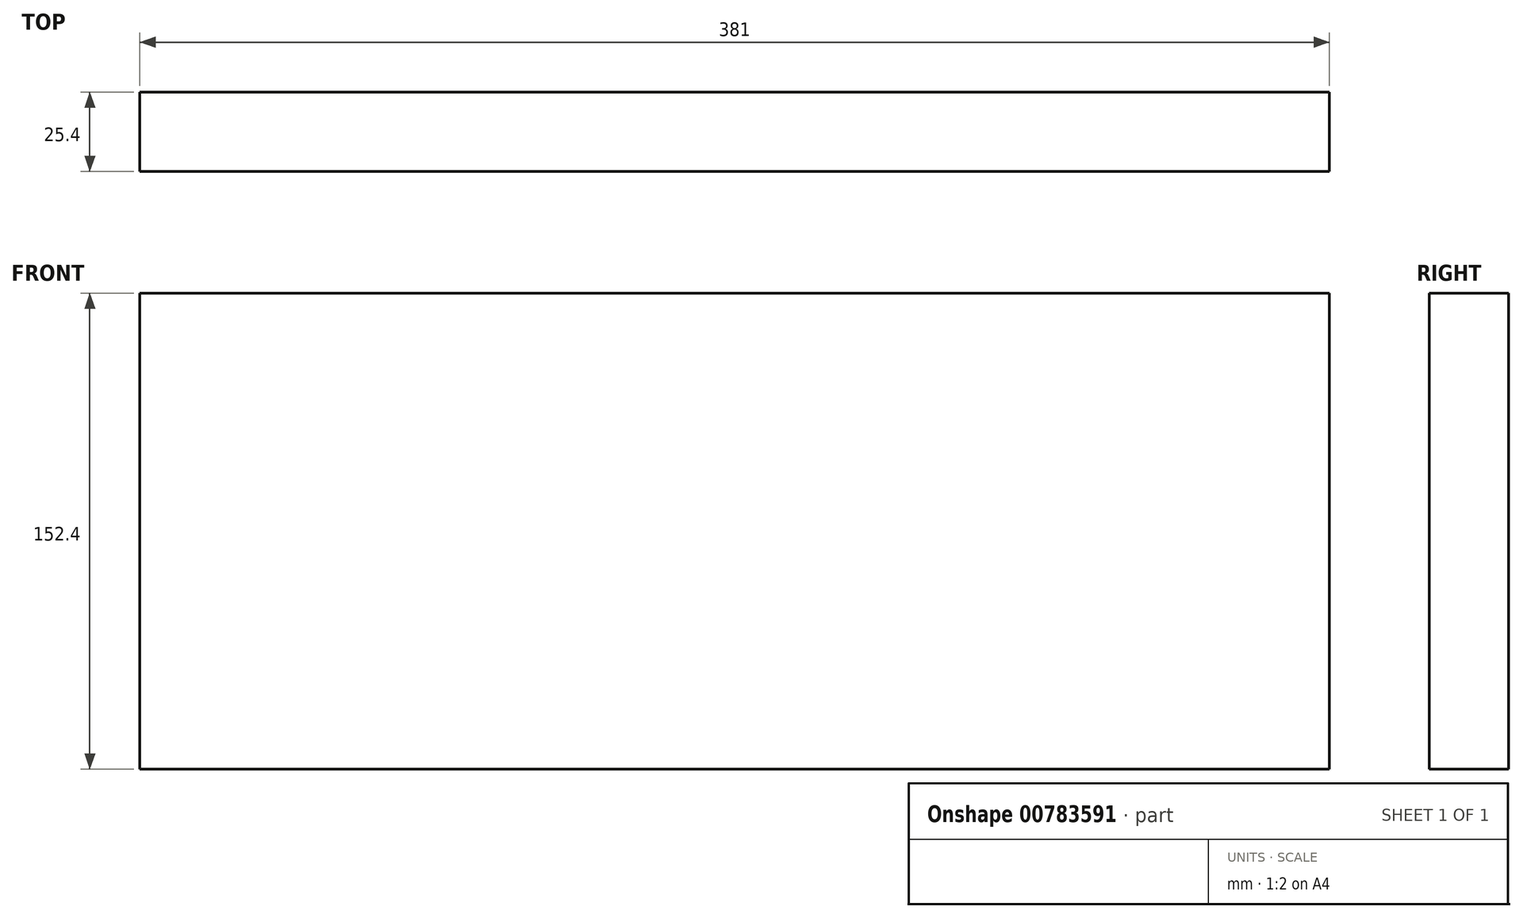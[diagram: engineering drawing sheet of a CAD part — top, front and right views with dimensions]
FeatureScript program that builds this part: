
annotation { "Feature Type Name" : "Feature", "Feature Type Description" : "" }
export const myFeature = defineFeature(function(context is Context, id is Id, definition is map)
    precondition{}
    {
        {
            var Q0;
            Q0=qCreatedBy(makeId("Front.planeOp"),FACE);
            var sketch = newSketch(context, id + "F0", { "sketchPlane" : qUnion([Q0])});
            skLineSegment(sketch, "E0.bottom", {"start": v(0, 0) * mm, "end": v(381, 0) * mm});
            skLineSegment(sketch, "E0.top", {"start": v(0, 152.4) * mm, "end": v(381, 152.4) * mm});
            skLineSegment(sketch, "E0.left", {"start": v(0, 0) * mm, "end": v(0, 152.4) * mm});
            skLineSegment(sketch, "E0.right", {"start": v(381, 0) * mm, "end": v(381, 152.4) * mm});
            skSolve(sketch);
        }
        {
            var Q0;
            Q0=makeQuery(id+"F0.imprint","IMPRINT",FACE,{"disambiguationData":[TD([[makeQuery(id+"F0.imprint","IMPRINT",EDGE,{"derivedFrom":sQuery(id+"F0.wireOp",EDGE,"E0.bottom")}),1.0]])]});
            extrude(context, id + "F1", {"entities" : qUnion([Q0]), "depth" : 25.4 * mm, "offsetDistance" : 25.4 * mm});
        }
    });
